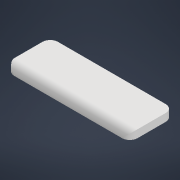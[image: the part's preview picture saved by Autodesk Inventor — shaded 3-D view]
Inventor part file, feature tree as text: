
AUTODESK INVENTOR PART (.ipt)
format: ipt  version: 2022 (Build 260153000, 153)  size: 99,328 bytes
history: native  units: mm
features: other x1, extrude x1, fillet x1, sketch x1
ambient origin geometry x8: Origin, YZ Plane, XZ Plane, XY Plane, X Axis, Y Axis, Z Axis, Center Point
bodies: Body1 (feature_tree)
feature tree (4):
  other  "Твердое тело1"
  extrude  "Выдавливание1"  Depth=480.0mm
  fillet  "Сопряжение1"  Radius=170.0mm
  sketch  "Эскиз1"
